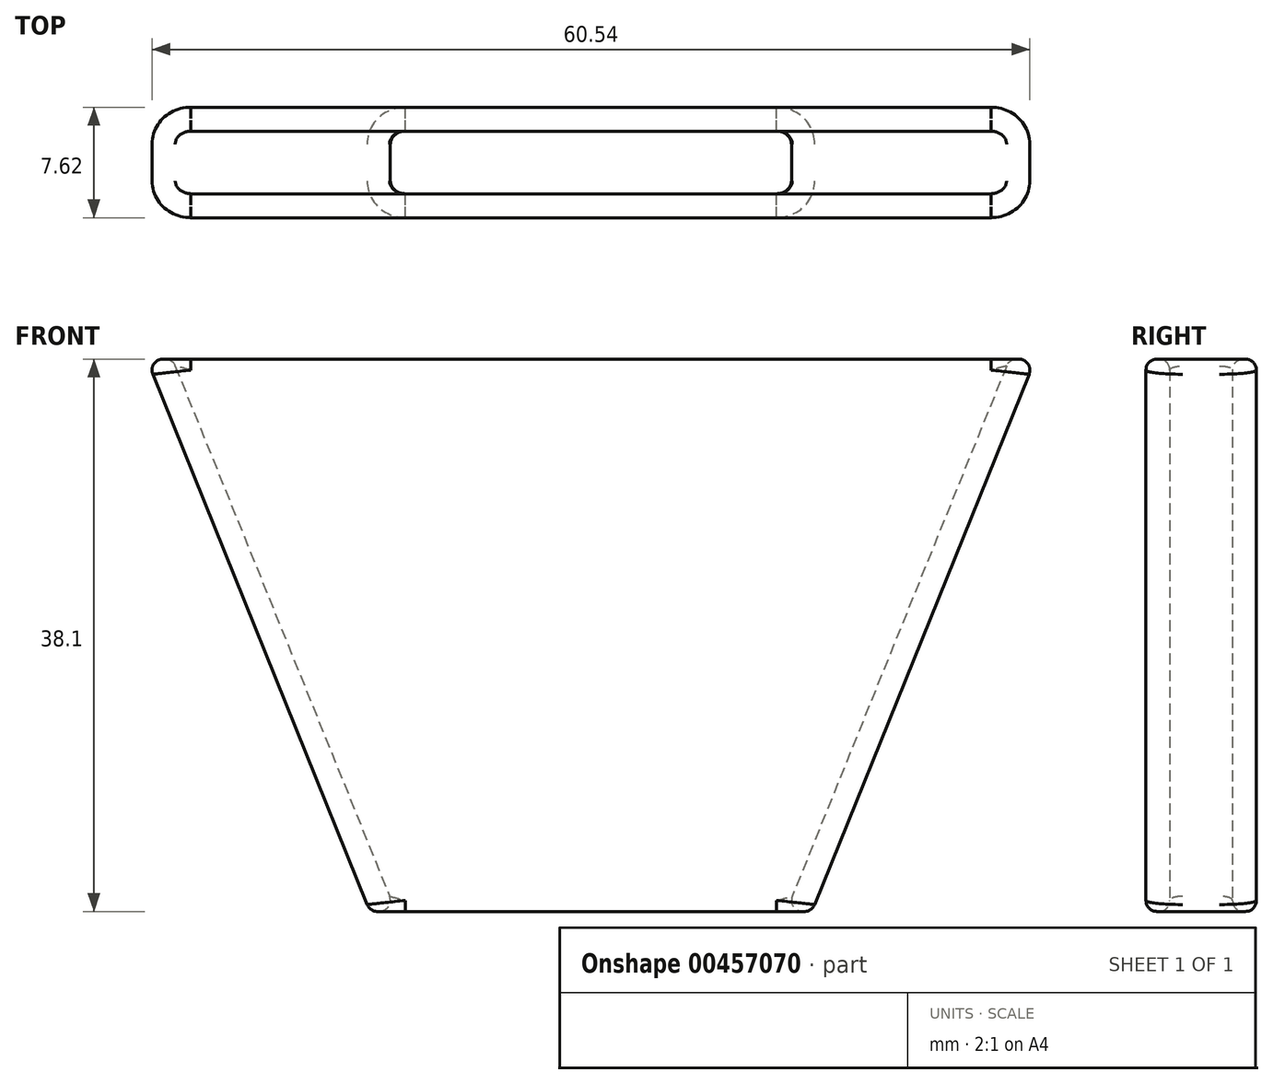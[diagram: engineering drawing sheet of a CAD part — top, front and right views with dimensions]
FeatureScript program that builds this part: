
annotation { "Feature Type Name" : "Feature", "Feature Type Description" : "" }
export const myFeature = defineFeature(function(context is Context, id is Id, definition is map)
    precondition{}
    {
        {
            var Q0;
            Q0=qCreatedBy(makeId("Front.planeOp"),FACE);
            var sketch = newSketch(context, id + "F0", { "sketchPlane" : qUnion([Q0])});
            skLineSegment(sketch, "E0", {"start": v(30.63, 0) * mm, "end": v(15.24, -38.1) * mm});
            skLineSegment(sketch, "E1.MirrorCS", {"start": v(-30.63, 0) * mm, "end": v(-15.24, -38.1) * mm});
            skLineSegment(sketch, "E2", {"start": v(-30.63, 0) * mm, "end": v(30.63, 0) * mm});
            skLineSegment(sketch, "E3", {"start": v(15.24, -38.1) * mm, "end": v(-15.24, -38.1) * mm});
            skLineSegment(sketch, "E4", {"start": v(0, 0) * mm, "end": v(0, -46.38) * mm, "construction": true});
            skSolve(sketch);
        }
        {
            var Q0;
            Q0 = qSketchRegion(id + "F0", true);
            extrude(context, id + "F1", {"entities" : qUnion([Q0]), "endBound" : BoundingType.SYMMETRIC, "depth" : 7.62 * mm});
        }
        {
            var Q0;
            Q0=makeQuery(id+"F1.opExtrude","CAP_EDGE",EDGE,{"disambiguationData":[OSD([sQuery(id+"F0.wireOp",EDGE,"E0")])],"isStart":true});
            var Q1;
            Q1=makeQuery(id+"F1.opExtrude","CAP_EDGE",EDGE,{"disambiguationData":[OSD([sQuery(id+"F0.wireOp",EDGE,"E0")])],"isStart":false});
            var Q2;
            Q2=makeQuery(id+"F1.opExtrude","CAP_EDGE",EDGE,{"disambiguationData":[OSD([sQuery(id+"F0.wireOp",EDGE,"E1.MirrorCS")])],"isStart":true});
            var Q3;
            Q3=makeQuery(id+"F1.opExtrude","CAP_EDGE",EDGE,{"disambiguationData":[OSD([sQuery(id+"F0.wireOp",EDGE,"E1.MirrorCS")])],"isStart":false});
            fillet(context, id + "F2", {"entities" : qUnion([Q0, Q1, Q2, Q3]), "radius" : 2.54 * mm, "tangentPropagation" : true, "allowEdgeOverflow" : false});
        }
        {
            var Q0;
            Q0=makeQuery(id+"F1.opExtrude","SWEPT_FACE",FACE,{"disambiguationData":[OSD([sQuery(id+"F0.wireOp",EDGE,"E2")])]});
            var Q1;
            Q1=makeQuery(id+"F1.opExtrude","SWEPT_FACE",FACE,{"disambiguationData":[OSD([sQuery(id+"F0.wireOp",EDGE,"E3")])]});
            shell(context, id + "F3", {"entities" : qUnion([Q0, Q1]), "thickness" : 1.65 * mm});
        }
        {
            var Q0;
            Q0=makeQuery(id+"F1.opExtrude","CAP_EDGE",EDGE,{"disambiguationData":[OSD([sQuery(id+"F0.wireOp",EDGE,"E2")])],"isStart":true});
            var Q1;
            {var subQ0=sQuery(id+"F0.wireOp",EDGE,"E2");Q1=makeQuery(id+"F3.opShell","OFFSET_EDGE",EDGE,{"disambiguationData":[OSD([subQ0]),TDD([makeQuery(id+"F1.opExtrude","CAP_EDGE",EDGE,{"disambiguationData":[OSD([subQ0])],"isStart":true})])]});}
            var Q2;
            Q2=makeQuery(id+"F1.opExtrude","CAP_EDGE",EDGE,{"disambiguationData":[OSD([sQuery(id+"F0.wireOp",EDGE,"E3")])],"isStart":true});
            var Q3;
            {var subQ0=sQuery(id+"F0.wireOp",EDGE,"E3");Q3=makeQuery(id+"F3.opShell","OFFSET_EDGE",EDGE,{"disambiguationData":[OSD([subQ0]),TDD([makeQuery(id+"F1.opExtrude","CAP_EDGE",EDGE,{"disambiguationData":[OSD([subQ0])],"isStart":true})])]});}
            fillet(context, id + "F4", {"entities" : qUnion([Q0, Q1, Q2, Q3]), "radius" : 0.76 * mm, "tangentPropagation" : true, "allowEdgeOverflow" : false});
        }
        {
            var Q0;
            Q0=qCreatedBy(makeId("Front.planeOp"),FACE);
            cPlane(context, id + "F5", {"entities" : qUnion([Q0]), "cplaneType" : CPlaneType.OFFSET, "offset" : 101.6 * mm, "width" : 152.4 * mm, "height" : 152.4 * mm});
        }
        {
            var Q0;
            {var subQ0=sQuery(id+"F0.wireOp",EDGE,"E3");var subQ1=sQuery(id+"F0.wireOp",EDGE,"E2");var subQ2=sQuery(id+"F0.wireOp",EDGE,"E1.MirrorCS");var subQ3=sQuery(id+"F0.wireOp",EDGE,"E0");Q0=makeQuery(id+"F3.opShell","OFFSET_FACE",FACE,{"disambiguationData":[OSD([subQ3,subQ2,subQ1,subQ0]),TDD([makeQuery(id+"F1.opExtrude","CAP_FACE",FACE,{"disambiguationData":[OSD([subQ3,subQ2,subQ1,subQ0])],"isStart":false})])]});}
            var sketch = newSketch(context, id + "F6", { "sketchPlane" : qUnion([Q0])});
            skLineSegment(sketch, "E5", {"start": v(0, 0) * mm, "end": v(0, 33.27) * mm, "construction": true});
            skSolve(sketch);
        }
    });
